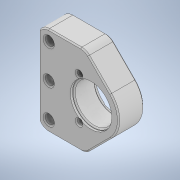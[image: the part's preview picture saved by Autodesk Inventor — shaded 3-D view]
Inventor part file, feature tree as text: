
AUTODESK INVENTOR PART (.ipt)
format: ipt  version: 2020 (Build 240168000, 168)  size: 258,048 bytes
history: native  units: in
note: dims shown in document units (in); Inventor stores cm internally (conversion verified against a paired STEP export)
features: extrude x4, sketch x4, chamfer x2, fillet x1
ambient origin geometry x8: Origin, YZ Plane, XZ Plane, XY Plane, X Axis, Y Axis, Z Axis, Center Point
bodies: Solid1 (feature_tree)
feature tree (11):
  extrude  "Extrusion1"  Depth=1.0in
  fillet  "Fillet1"  Radius=0.2656in
  extrude  "Extrusion2"  Depth=0.3198in
  extrude  "Extrusion3"  Depth=0.3198in
  extrude  "Extrusion4"  TaperAngle=45.0deg  [1 undecoded]
  chamfer  "Chamfer1"  Angle=45.0deg  [1 undecoded]
  chamfer  "Chamfer2"  Distance=0.75in
  sketch  "Sketch1"  dims[d0=1.126in d1=1.0in d2=0.2656in]
  sketch  "Sketch2"  dims[d4=1.1811in d6=1.0in d7=0.3937in d9=1.0in d11=0.3198in]
  sketch  "Sketch3"  dims[d12=0.3198in d13=0.3198in]
  sketch  "Sketch4"  dims[d14=0.813in d15=45.0deg d16=45.0deg d17=0.75in d18=0.0in d19=0.3198in d20=0.7105in d21=0.159in d22=120.0deg d23=1.1811in d25=360.0deg d27=0.0in d28=0.0in d29=1.226in d30=0.064in d31=0.0in d32=1.226in d33=0.064in d34=0.0in d35=0.035in d36=0.125in d37=45.0deg d43=1.225in d45=1.25in d46=0.6375in d47=2.0in d48=1.0in d49=135.0deg d50=0.375in d51=0.125in d52=0.125in d53=45.0deg]
note: 2 required parameter values undecoded (feature->parameter linkage not recoverable at this tier; creation-order binding heuristic only, values carry confidence <= 0.55)
